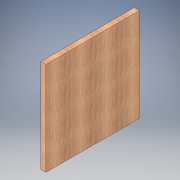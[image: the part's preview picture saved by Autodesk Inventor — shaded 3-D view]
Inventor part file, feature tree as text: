
AUTODESK INVENTOR PART (.ipt)
format: ipt  version: 2017 (Build 210142000, 142)  size: 111,104 bytes
history: native  units: in
note: dims shown in document units (in); Inventor stores cm internally (conversion verified against a paired STEP export)
features: extrude x1, sketch x1
ambient origin geometry x8: Origin, YZ Plane, XZ Plane, XY Plane, X Axis, Y Axis, Z Axis, Center Point
bodies: Solid1 (feature_tree)
feature tree (2):
  extrude  "Extrusion1"  Depth=36.0in
  sketch  "Sketch1"  dims[d0=2.0in d1=36.0in d2=36.0in d3=0.0in]
